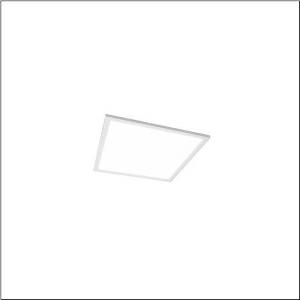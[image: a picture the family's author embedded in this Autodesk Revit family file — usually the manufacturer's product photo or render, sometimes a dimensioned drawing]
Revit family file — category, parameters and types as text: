
# Revit family: apollon_21_square_51mq13wd2313
name_source: partatom
category: Lighting Fixtures
units: mm (PartAtom-declared; Revit-internal decimal feet)

## family parameters
Cut with Voids When Loaded = No
Host = Face
Light Source = No
Part Type = Normal
Room Calculation Point = No
Round Connector Dimension = Use Diameter
Shared = No

## types (1)
- Apollon 21 square (1 x LED, 1700 lm, 15 W, 3000K)
    Apparent Load = 15 VA
    CIE Flux Codes = 59 88 97 100 100
    Color Rendering = 80
    Color Temperature = 3000K
    Default Elevation = 1800 mm
    Description = Apollon 21 square, office luminaire, primary optical cover: micro prismatic cover, of PMMA, CAT 2 (L<= 3000cd/m²), light emission: direct distribution, primary light characteristic: symmetric, installation type: lay-in mounting, LED, rated luminous flux: 1.700lm, luminous efficacy: 113lm/W, light colour: 830, colour temperature: 3000K, control gear: DALI 2, with terminal, 5-pole, mains connection: 220..240V, AC, 50/60Hz, rated input power: 15W, housing, of sheet steel, coated, pure white, length: 296mm, width: 296mm, height: 40mm, housing upper side, of sheet steel, galvanised, protection rating (complete): IP20, protection rating (lamp compartment, on room side): IP50, insulation class (complete): insulation class II (safety insulation), certification: CE, ENEC, permissible operating ambient temperature: -20..+40°C, packaging unit: 1 piece
    Height = 0 mm  [stored 0 ft]
    Lamp = 1 x LED
    Lamp Light Flux = 1700 lm
    Lamp Power = 15 W
    Lamp count = 1
    Length = 295 mm
    Luminous efficacy = 113 lm/W
    Manufacturer = Siteco
    ModVariant = No
    Model = 51MQ13WD2313
    Mounting Place = Ceiling
    Mounting Type = Recessed
    Number of Poles = 1
    OnlyDefault = Yes
    Power Factor = 1
    Product Name = Apollon 21 square
    Product group = office luminaire | ceiling recessed
    ProductGroupID = 400
    Protection Class = Protection class II
    Protection Degree = IP 20
    RLX_Detail_Level = 1
    RLX_Emergency_Light_Flux = 0 lm
    RLX_Emergency_Type = 0
    RLX_Emergency_Type_DB = No
    RlxData = <blob elided: 9081 chars, md5=8581fcd7>
    Socket = socket
    Standby Power = 0 W
    System Light Flux = 1700 lm
    System Power = 15 W
    Type Comments = Product without accessories
    Type Image = l_1291030.jpg
    URL = http://relux.com
    VarID = ---
    Voltage = 0 V
    Weight = 0.00 kg
    Width = 295 mm

note: [stored X ft] marks values corroborated as IEEE doubles in the binary element streams (Revit-internal decimal feet)

## geometry (parser evidence)
native form markers: Sweep x10
no freeform markers — native parametric forms only
